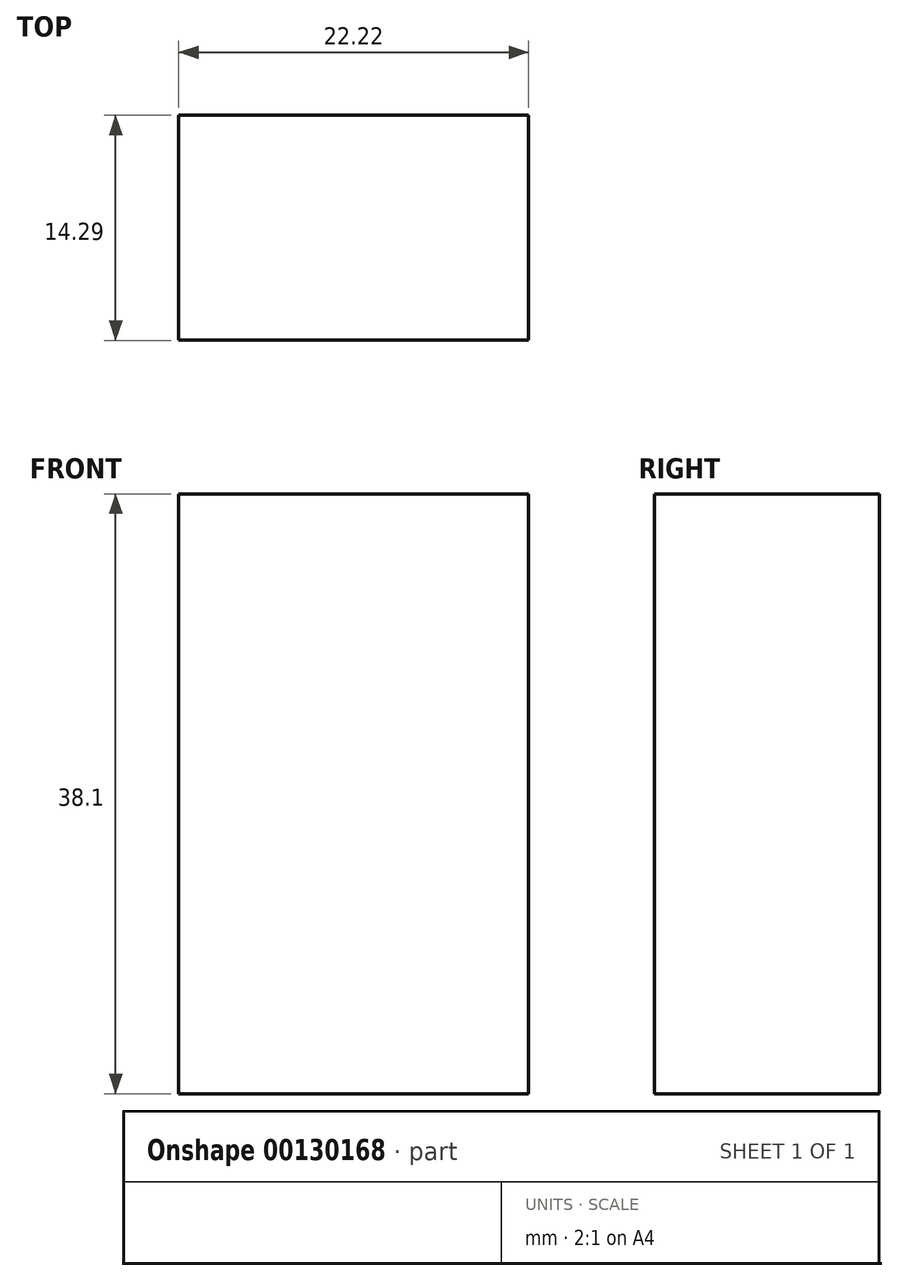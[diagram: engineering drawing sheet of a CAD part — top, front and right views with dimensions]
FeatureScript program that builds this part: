
annotation { "Feature Type Name" : "Feature", "Feature Type Description" : "" }
export const myFeature = defineFeature(function(context is Context, id is Id, definition is map)
    precondition{}
    {
        {
            var Q0;
            Q0=qCreatedBy(makeId("Front.planeOp"),FACE);
            var sketch = newSketch(context, id + "F0", { "sketchPlane" : qUnion([Q0])});
            skLineSegment(sketch, "E0.bottom", {"start": v(-15.66, 26.95) * mm, "end": v(6.56, 26.95) * mm});
            skLineSegment(sketch, "E0.top", {"start": v(-15.66, -11.15) * mm, "end": v(6.56, -11.15) * mm});
            skLineSegment(sketch, "E0.left", {"start": v(-15.66, 26.95) * mm, "end": v(-15.66, -11.15) * mm});
            skLineSegment(sketch, "E0.right", {"start": v(6.56, 26.95) * mm, "end": v(6.56, -11.15) * mm});
            skSolve(sketch);
        }
        {
            var Q0;
            Q0=makeQuery(id+"F0.imprint","IMPRINT",FACE,{"disambiguationData":[TD([[makeQuery(id+"F0.imprint","IMPRINT",EDGE,{"derivedFrom":sQuery(id+"F0.wireOp",EDGE,"E0.bottom")}),-1.0]])]});
            extrude(context, id + "F1", {"entities" : qUnion([Q0]), "depth" : 14.29 * mm});
        }
    });
